# Revit family: Door-Fire_AlarmGard_BetweenJambMount_Cookson
name_source: partatom
category: Doors
revit_build: Autodesk Revit MEP 2013 (Build: 20130531_2115(x64)
units: mm (PartAtom-declared; Revit-internal decimal feet)

## types (4) — shared parameters
04 CSI = 08 33 00
95 CSI = 08330
Assembly Code = B2030410
Coil Dimension Note = 14In to 25In -  Consult Cornell when dimensions are critical.
Description = Rated physical fire barriers, also security and access control. Not for part of required means of egress.
Distributor Locator = http://www.cooksondoor.com
From Coil Side Operate on Left = No
From Coil Side Operate on Right = Yes
Function = Interior
Height = 8' - 0"
Jamb Dimension Note = 7 3/4In to 11In wide. Consult Cornell when dimensions are critical.
LEED Information = http://www.cornelliron.com
Listings = UL Classified 4, 3, 1 ½, 1 and ¾ hour labels. Factory Mutual approval listing.
Manufacturer = CornellCookson,Inc.
Model = ERD10
Mounting = Between Jambs
Operator Height = 5' - 4"
Operator Width = 5' - 7 1/2"
Optional Powder Coated Finish, standard RAL colors, Galv. Steel only = No
Representative Disclaimer = Cookson products are sold and installed through a nationwide network of independent distributors.
Revit Object Download Link = http://cornellcookson.smartbim.com
Sizing Disclaimer = 30’ wide, 30’ high standard construction. Large Openings to 50’ wide, 40’ high consult factory.
Smoke Control = UL leakage rated assembly “S” label available.
Subcategory = Overhead Doors
URL = http://www.cooksondoor.com
URL CAD = http://www.cooksondoor.com
URL Photographs = http://www.cooksondoor.com
URL Specifications = http://www.cooksondoor.com
Wall Closure = By host
Wall Construction = Masonry or Steel
Width = 6' - 0"
Windload = A full range of specific wind load requirements available- consult Cornell.

## per-type parameters (varying)
| type | Bottom Bar | Chain | Curtain 2 5/8" slat | Guides | Hood | Motor | Operator |
| Hand-Chain Operated, Galvanized Steel | Galvanized or plain steel(non curtain components) | Yes | Galvanized steel (curtain only) | Galvanized or plain steel(non curtain components) | Galvanized or plain steel(non curtain components) | No | Operator : Hand-Chain |
| Hand-Chain Operated, Stainless Steel | Stainless steel (non-curtain components) | Yes | Stainless steel (curtain only) | Stainless steel (non-curtain components) | Stainless steel (non-curtain components) | No | Operator : Hand-Chain |
| Motor Operated, Galvanized Steel | Galvanized or plain steel(non curtain components) | No | Galvanized steel (curtain only) | Galvanized or plain steel(non curtain components) | Galvanized or plain steel(non curtain components) | Yes | Operator : Motor Operator |
| Motor Operated, Stainless Steel | Stainless steel (non-curtain components) | No | Stainless steel (curtain only) | Stainless steel (non-curtain components) | Stainless steel (non-curtain components) | Yes | Operator : Motor Operator |

## geometry (parser evidence)
native form markers: Blend x8, Sweep x13
no freeform markers — native parametric forms only
